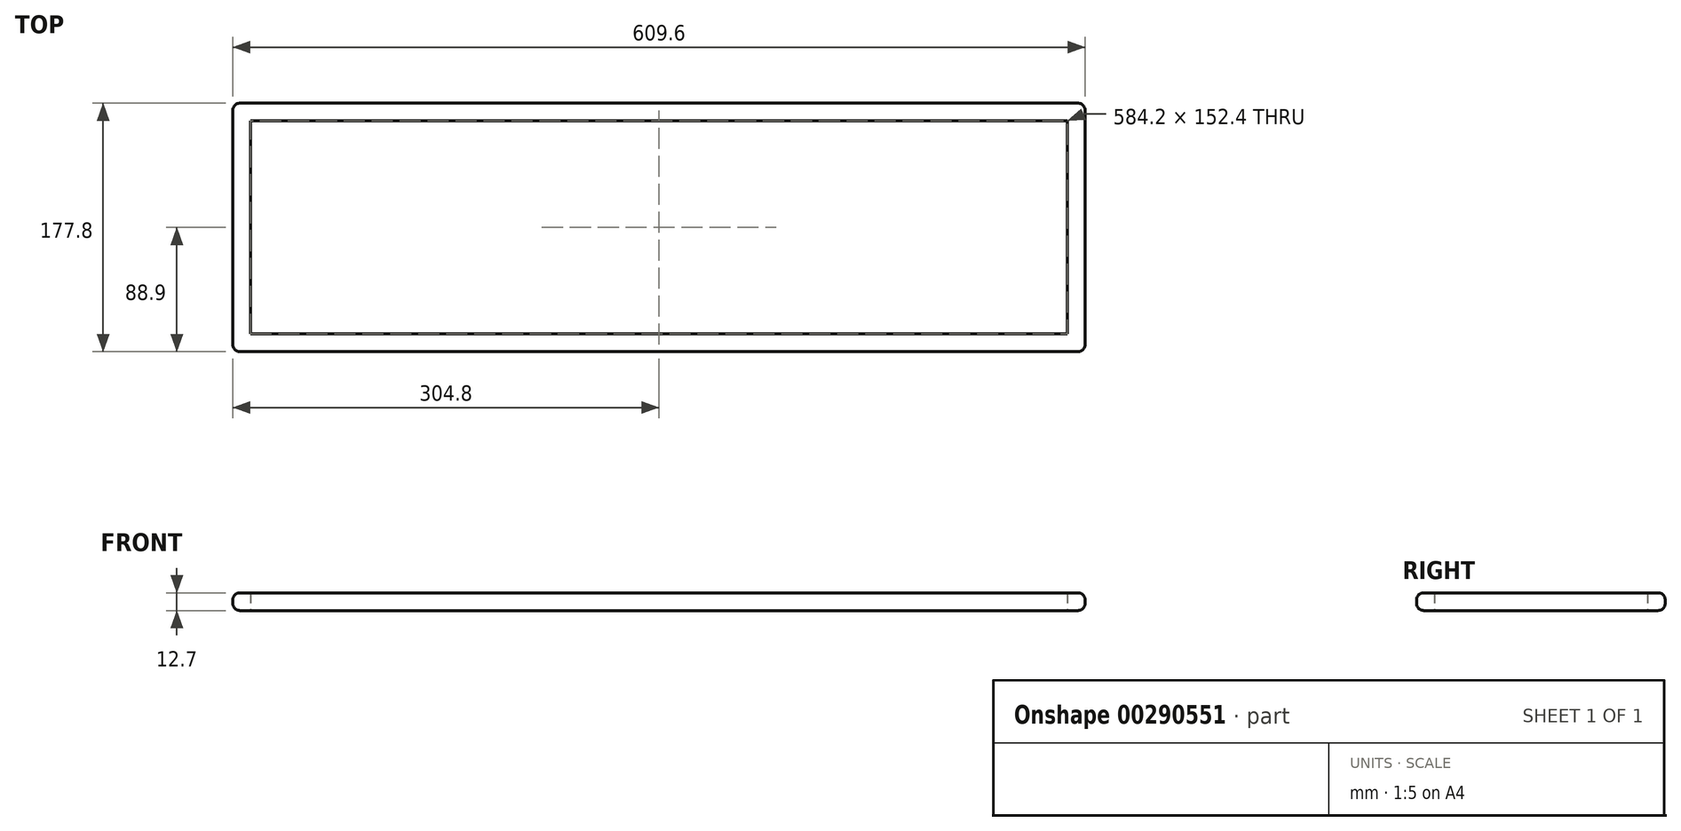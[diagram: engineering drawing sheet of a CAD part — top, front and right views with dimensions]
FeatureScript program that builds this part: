
annotation { "Feature Type Name" : "Feature", "Feature Type Description" : "" }
export const myFeature = defineFeature(function(context is Context, id is Id, definition is map)
    precondition{}
    {
        {
            var Q0;
            Q0=qCreatedBy(makeId("Top.planeOp"),FACE);
            var sketch = newSketch(context, id + "F0", { "sketchPlane" : qUnion([Q0])});
            skLineSegment(sketch, "E0.bottom", {"start": v(-304.8, 88.9) * mm, "end": v(304.8, 88.9) * mm});
            skLineSegment(sketch, "E0.top", {"start": v(-304.8, -88.9) * mm, "end": v(304.8, -88.9) * mm});
            skLineSegment(sketch, "E0.left", {"start": v(-304.8, 88.9) * mm, "end": v(-304.8, -88.9) * mm});
            skLineSegment(sketch, "E0.right", {"start": v(304.8, 88.9) * mm, "end": v(304.8, -88.9) * mm});
            skPoint(sketch, "E0.middle", {"position": v(0, 0) * mm});
            skLineSegment(sketch, "E1.bottom", {"start": v(-292.1, 76.2) * mm, "end": v(292.1, 76.2) * mm});
            skLineSegment(sketch, "E1.top", {"start": v(-292.1, -76.2) * mm, "end": v(292.1, -76.2) * mm});
            skLineSegment(sketch, "E1.left", {"start": v(-292.1, 76.2) * mm, "end": v(-292.1, -76.2) * mm});
            skLineSegment(sketch, "E1.right", {"start": v(292.1, 76.2) * mm, "end": v(292.1, -76.2) * mm});
            skSolve(sketch);
        }
        {
            var Q0;
            Q0 = qSketchRegion(id + "F0", true);
            extrude(context, id + "F1", {"entities" : qUnion([Q0]), "depth" : 12.7 * mm});
        }
        {
            var Q0;
            Q0=makeQuery(id+"F1.opExtrude","CAP_EDGE",EDGE,{"disambiguationData":[OSD([sQuery(id+"F0.wireOp",EDGE,"E0.top")])],"isStart":false});
            var Q1;
            Q1=makeQuery(id+"F1.opExtrude","CAP_EDGE",EDGE,{"disambiguationData":[OSD([sQuery(id+"F0.wireOp",EDGE,"E0.left")])],"isStart":false});
            var Q2;
            Q2=makeQuery(id+"F1.opExtrude","CAP_EDGE",EDGE,{"disambiguationData":[OSD([sQuery(id+"F0.wireOp",EDGE,"E0.right")])],"isStart":true});
            var Q3;
            Q3=makeQuery(id+"F1.opExtrude","CAP_EDGE",EDGE,{"disambiguationData":[OSD([sQuery(id+"F0.wireOp",EDGE,"E0.bottom")])],"isStart":false});
            var Q4;
            Q4=makeQuery(id+"F1.opExtrude","SWEPT_EDGE",EDGE,{"disambiguationData":[OSD([sQuery(id+"F0.wireOp",EDGE,"E0.bottom"),sQuery(id+"F0.wireOp",EDGE,"E0.right")])]});
            var Q5;
            Q5=makeQuery(id+"F1.opExtrude","SWEPT_EDGE",EDGE,{"disambiguationData":[OSD([sQuery(id+"F0.wireOp",EDGE,"E0.top"),sQuery(id+"F0.wireOp",EDGE,"E0.right")])]});
            var Q6;
            Q6=makeQuery(id+"F1.opExtrude","SWEPT_EDGE",EDGE,{"disambiguationData":[OSD([sQuery(id+"F0.wireOp",EDGE,"E0.top"),sQuery(id+"F0.wireOp",EDGE,"E0.left")])]});
            var Q7;
            Q7=makeQuery(id+"F1.opExtrude","SWEPT_EDGE",EDGE,{"disambiguationData":[OSD([sQuery(id+"F0.wireOp",EDGE,"E0.bottom"),sQuery(id+"F0.wireOp",EDGE,"E0.left")])]});
            var Q8;
            Q8=makeQuery(id+"F1.opExtrude","CAP_EDGE",EDGE,{"disambiguationData":[OSD([sQuery(id+"F0.wireOp",EDGE,"E0.right")])],"isStart":false});
            var Q9;
            Q9=makeQuery(id+"F1.opExtrude","CAP_EDGE",EDGE,{"disambiguationData":[OSD([sQuery(id+"F0.wireOp",EDGE,"E0.top")])],"isStart":true});
            var Q10;
            Q10=makeQuery(id+"F1.opExtrude","CAP_EDGE",EDGE,{"disambiguationData":[OSD([sQuery(id+"F0.wireOp",EDGE,"E0.bottom")])],"isStart":true});
            var Q11;
            Q11=makeQuery(id+"F1.opExtrude","CAP_EDGE",EDGE,{"disambiguationData":[OSD([sQuery(id+"F0.wireOp",EDGE,"E0.left")])],"isStart":true});
            fillet(context, id + "F2", {"entities" : qUnion([Q0, Q1, Q2, Q3, Q4, Q5, Q6, Q7, Q8, Q9, Q10, Q11]), "radius" : 5.08 * mm, "tangentPropagation" : true, "allowEdgeOverflow" : false});
        }
    });
